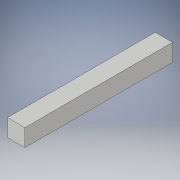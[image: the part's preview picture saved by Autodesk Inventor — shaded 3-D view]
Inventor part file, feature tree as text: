
AUTODESK INVENTOR PART (.ipt)
format: ipt  version: 2017 (Build 210142000, 142)  size: 89,600 bytes
history: native  units: in
note: dims shown in document units (in); Inventor stores cm internally (conversion verified against a paired STEP export)
features: extrude x1, sketch x1
ambient origin geometry x8: Origin, YZ Plane, XZ Plane, XY Plane, X Axis, Y Axis, Z Axis, Center Point
bodies: Solid1 (feature_tree)
feature tree (2):
  extrude  "Extrusion1"  Depth=17.0in
  sketch  "Sketch1"  dims[d0=2.0in d1=17.0in d2=2.0in d3=0.0in]
